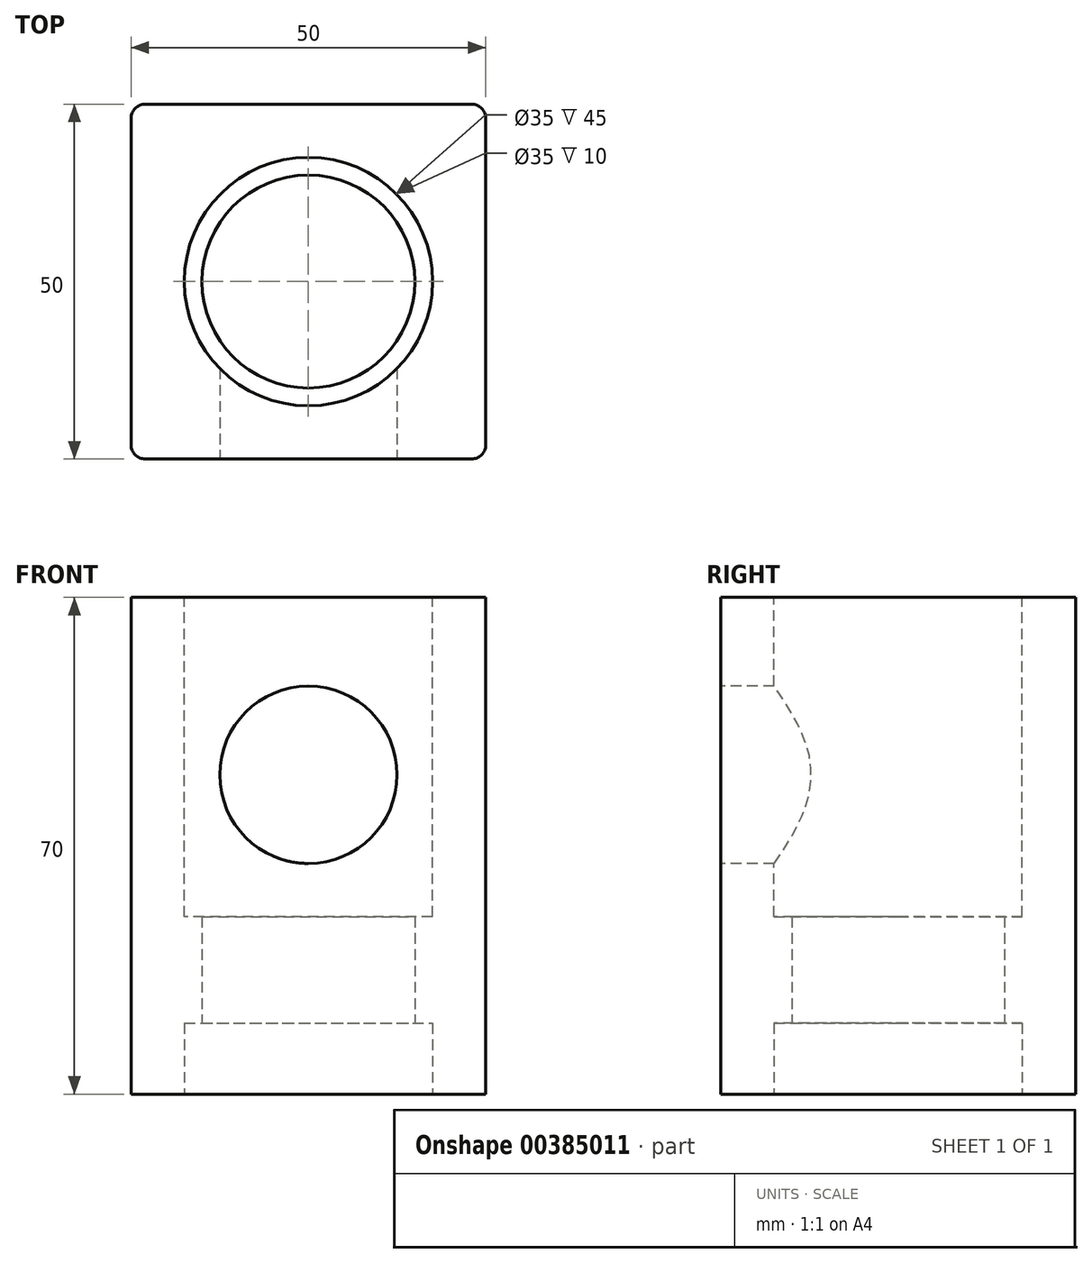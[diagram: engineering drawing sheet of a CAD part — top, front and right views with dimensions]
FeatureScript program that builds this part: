
annotation { "Feature Type Name" : "Feature", "Feature Type Description" : "" }
export const myFeature = defineFeature(function(context is Context, id is Id, definition is map)
    precondition{}
    {
        {
            var Q0;
            Q0=qCreatedBy(makeId("Top.planeOp"),FACE);
            var sketch = newSketch(context, id + "F0", { "sketchPlane" : qUnion([Q0])});
            skCircle(sketch, "E0", {"center": v(0, 0) * mm, "radius": 15 * mm});
            skLineSegment(sketch, "E1.bottom", {"start": v(25, -25) * mm, "end": v(-25, -25) * mm});
            skLineSegment(sketch, "E1.top", {"start": v(25, 25) * mm, "end": v(-25, 25) * mm});
            skLineSegment(sketch, "E1.left", {"start": v(25, -25) * mm, "end": v(25, 25) * mm});
            skLineSegment(sketch, "E1.right", {"start": v(-25, -25) * mm, "end": v(-25, 25) * mm});
            skSolve(sketch);
        }
        {
            var Q0;
            Q0 = qSketchRegion(id + "F0", true);
            extrude(context, id + "F1", {"entities" : qUnion([Q0]), "depth" : 70 * mm});
        }
        {
            var Q0;
            Q0=makeQuery(id+"F1.opExtrude","SWEPT_FACE",FACE,{"disambiguationData":[OSD([sQuery(id+"F0.wireOp",EDGE,"E1.bottom")])]});
            var sketch = newSketch(context, id + "F2", { "sketchPlane" : qUnion([Q0])});
            skCircle(sketch, "E2", {"center": v(0, 45) * mm, "radius": 12.5 * mm});
            skSolve(sketch);
        }
        {
            var Q0;
            Q0 = qSketchRegion(id + "F2", true);
            extrude(context, id + "F3", {"entities" : qUnion([Q0]), "operationType" : NewBodyOperationType.REMOVE, "oppositeDirection" : true, "depth" : 25 * mm});
        }
        {
            var Q0;
            Q0=makeQuery(id+"F1.opExtrude","CAP_FACE",FACE,{"disambiguationData":[OSD([sQuery(id+"F0.wireOp",EDGE,"E0"),sQuery(id+"F0.wireOp",EDGE,"E1.bottom"),sQuery(id+"F0.wireOp",EDGE,"E1.top"),sQuery(id+"F0.wireOp",EDGE,"E1.left"),sQuery(id+"F0.wireOp",EDGE,"E1.right")])],"isStart":false});
            var sketch = newSketch(context, id + "F4", { "sketchPlane" : qUnion([Q0])});
            skCircle(sketch, "E3", {"center": v(0, 0) * mm, "radius": 17.5 * mm});
            skSolve(sketch);
        }
        {
            var Q0;
            Q0 = qSketchRegion(id + "F4", true);
            extrude(context, id + "F5", {"entities" : qUnion([Q0]), "operationType" : NewBodyOperationType.REMOVE, "oppositeDirection" : true, "depth" : 45 * mm});
        }
        {
            var Q0;
            Q0=makeQuery(id+"F1.opExtrude","CAP_FACE",FACE,{"disambiguationData":[OSD([sQuery(id+"F0.wireOp",EDGE,"E0"),sQuery(id+"F0.wireOp",EDGE,"E1.bottom"),sQuery(id+"F0.wireOp",EDGE,"E1.top"),sQuery(id+"F0.wireOp",EDGE,"E1.left"),sQuery(id+"F0.wireOp",EDGE,"E1.right")])],"isStart":true});
            var sketch = newSketch(context, id + "F6", { "sketchPlane" : qUnion([Q0])});
            skCircle(sketch, "E4", {"center": v(0, 0) * mm, "radius": 17.5 * mm});
            skSolve(sketch);
        }
        {
            var Q0;
            Q0 = qSketchRegion(id + "F6", true);
            extrude(context, id + "F7", {"entities" : qUnion([Q0]), "operationType" : NewBodyOperationType.REMOVE, "oppositeDirection" : true, "depth" : 10 * mm});
        }
        {
            var Q0;
            Q0=makeQuery(id+"F1.opExtrude","SWEPT_EDGE",EDGE,{"disambiguationData":[OSD([sQuery(id+"F0.wireOp",EDGE,"E1.bottom"),sQuery(id+"F0.wireOp",EDGE,"E1.right")])]});
            var Q1;
            Q1=makeQuery(id+"F1.opExtrude","SWEPT_EDGE",EDGE,{"disambiguationData":[OSD([sQuery(id+"F0.wireOp",EDGE,"E1.bottom"),sQuery(id+"F0.wireOp",EDGE,"E1.left")])]});
            var Q2;
            Q2=makeQuery(id+"F1.opExtrude","SWEPT_EDGE",EDGE,{"disambiguationData":[OSD([sQuery(id+"F0.wireOp",EDGE,"E1.top"),sQuery(id+"F0.wireOp",EDGE,"E1.left")])]});
            var Q3;
            Q3=makeQuery(id+"F1.opExtrude","SWEPT_EDGE",EDGE,{"disambiguationData":[OSD([sQuery(id+"F0.wireOp",EDGE,"E1.top"),sQuery(id+"F0.wireOp",EDGE,"E1.right")])]});
            fillet(context, id + "F8", {"entities" : qUnion([Q0, Q1, Q2, Q3]), "radius" : 2 * mm, "tangentPropagation" : true, "allowEdgeOverflow" : false});
        }
    });
